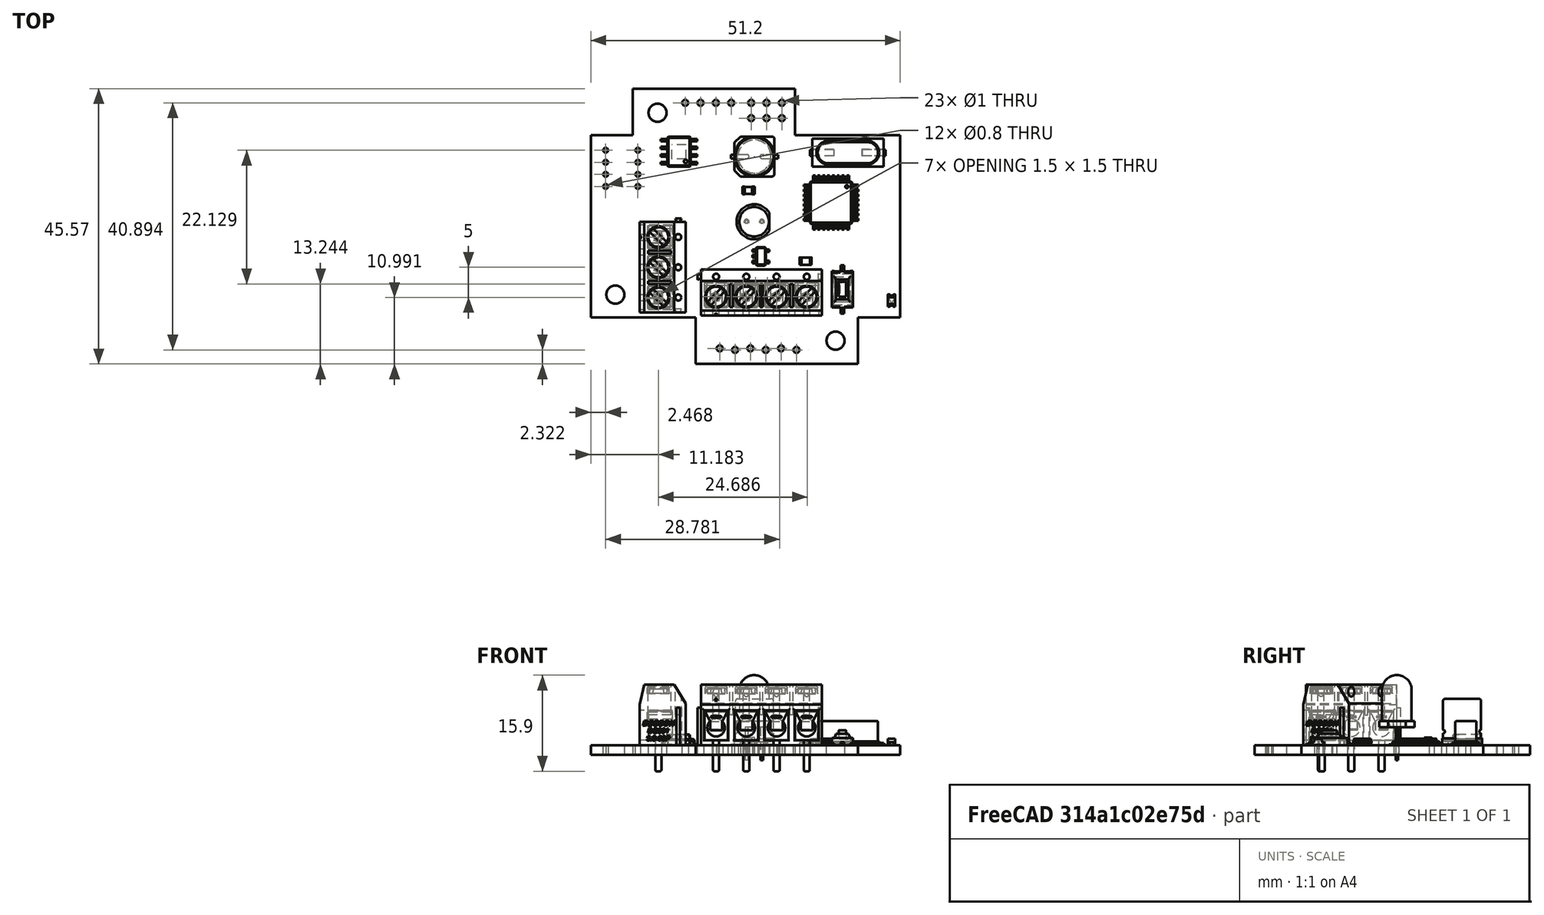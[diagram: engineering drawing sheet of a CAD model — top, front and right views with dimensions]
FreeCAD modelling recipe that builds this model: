
FCSTD DOCUMENT  (FreeCAD 0.19R24291 (Git))
Label: SolarSensorATMEGA328_PCB_freeCAD
License: All rights reserved
LicenseURL: http://en.wikipedia.org/wiki/All_rights_reserved
objects: App::Link×16, Part::Feature×13, App::Part×6, PartDesign::CoordinateSystem×1, Sketcher::SketchObject×1
note: 15 computed .brp shape members not serialized (recipe doc carries the construction recipe); baked Part::Feature solids carry a one-line shape summary decoded from their .brp

FEATURE [PartDesign::CoordinateSystem] Local_CS_ab9b
  AttacherType = Attacher::AttachEngine3D
FEATURE [Part::Feature] Pcb_ab9b
  shape: bbox 51.19 x 45.57 x 1.6 mm, 54 faces (baked)
FEATURE [Sketcher::SketchObject] PCB_Sketch_ab9b
  FullyConstrained = true
FEATURE [App::Part] Board_Geoms_ab9b
  Group = -> [Local_CS_ab9b,Pcb_ab9b,PCB_Sketch_ab9b]
  Origin = -> Origin
FEATURE [Part::Feature] Shape  label="SW2_SW_SPST_CK_RS282G05A3_60F30811"
  Placement = pos=(134.468,-118.745,0) rot=(0,0,-1;1.5708rad)
  shape: bbox 3.5 x 8 x 2.5 mm, 109 faces (baked)
FEATURE [App::Link] SW2_SW_SPST_CK_RS282G05A3_60F30811_ln_  label="SW1_SW_SPST_CK_RS282G05A3_60F354E5"
  LinkPlacement = pos=(139.065,-118.745,0) rot=(0,0,-1;1.5708rad)
  LinkedObject = -> Shape
  Placement = pos=(139.065,-118.745,0) rot=(0,0,-1;1.5708rad)
FEATURE [Part::Feature] Shape001  label="D2_LED_0805_2012Metric_Castellated_60F53ACF"
  Placement = pos=(142.621,-120.617,0) rot=(0,0,1;1.5708rad)
  shape: bbox 1.25 x 2 x 1.1 mm, 38 faces (baked)
FEATURE [Part::Feature] Shape002  label="R7_R_0805_2012Metric_60F30805"
  Placement = pos=(128.397,-114.096,0) rot=(0,0,1;0rad)
  shape: bbox 2 x 1.2 x 0.45 mm, 26 faces (baked)
FEATURE [App::Link] R7_R_0805_2012Metric_60F30805_ln_  label="R1_R_0805_2012Metric_60F3722D"
  LinkPlacement = pos=(114.758,-112.949,0) rot=(0,0,-1;1.5708rad)
  LinkedObject = -> Shape002
  Placement = pos=(114.758,-112.949,0) rot=(0,0,-1;1.5708rad)
FEATURE [App::Link] R7_R_0805_2012Metric_60F30805_ln_001  label="R4_R_0805_2012Metric_60F37335"
  LinkPlacement = pos=(142.571,-113.589,0) rot=(0,0,-1;1.5708rad)
  LinkedObject = -> Shape002
  Placement = pos=(142.571,-113.589,0) rot=(0,0,-1;1.5708rad)
FEATURE [App::Link] R7_R_0805_2012Metric_60F30805_ln_002  label="R5_R_0805_2012Metric_60F373AA"
  LinkPlacement = pos=(134.443,-112.319,0) rot=(0,0,-1;1.5708rad)
  LinkedObject = -> Shape002
  Placement = pos=(134.443,-112.319,0) rot=(0,0,-1;1.5708rad)
FEATURE [App::Link] R7_R_0805_2012Metric_60F30805_ln_003  label="R6_R_0805_2012Metric_60F35493"
  LinkPlacement = pos=(128.448,-111.556,0) rot=(0,0,1;0rad)
  LinkedObject = -> Shape002
  Placement = pos=(128.448,-111.556,0) rot=(0,0,1;0rad)
FEATURE [App::Link] R7_R_0805_2012Metric_60F30805_ln_004  label="R2_R_0805_2012Metric_61BC8E5A"
  LinkPlacement = pos=(112.218,-112.949,0) rot=(0,0,-1;1.5708rad)
  LinkedObject = -> Shape002
  Placement = pos=(112.218,-112.949,0) rot=(0,0,-1;1.5708rad)
FEATURE [Part::Feature] Shape003  label="C7_C_0805_2012Metric_60F30728[2]"
  Placement = pos=(118.948,-102.389,0) rot=(0,0,1;3.14159rad)
  shape: bbox 2 x 1.25 x 1.25 mm, 28 faces (baked)
FEATURE [App::Link] C7_C_0805_2012Metric_60F30728_2__ln_  label="C8_C_0805_2012Metric_60F30734[2]"
  LinkPlacement = pos=(109.447,-120.467,0) rot=(0,0,1;1.5708rad)
  LinkedObject = -> Shape003
  Placement = pos=(109.447,-120.467,0) rot=(0,0,1;1.5708rad)
FEATURE [App::Link] C7_C_0805_2012Metric_60F30728_2__ln_001  label="C9_C_0805_2012Metric_60F30740[2]"
  LinkPlacement = pos=(139.883,-100.049,0) rot=(0,0,1;0rad)
  LinkedObject = -> Shape003
  Placement = pos=(139.883,-100.049,0) rot=(0,0,1;0rad)
FEATURE [App::Link] C7_C_0805_2012Metric_60F30728_2__ln_002  label="C10_C_0805_2012Metric_60F3074C[2]"
  LinkPlacement = pos=(126.338,-97.0992,0) rot=(0,0,1;1.5708rad)
  LinkedObject = -> Shape003
  Placement = pos=(126.338,-97.0992,0) rot=(0,0,1;1.5708rad)
FEATURE [App::Link] C7_C_0805_2012Metric_60F30728_2__ln_003  label="C1_C_0805_2012Metric_60F372F7[2]"
  LinkPlacement = pos=(117.248,-112.954,0) rot=(0,0,-1;1.5708rad)
  LinkedObject = -> Shape003
  Placement = pos=(117.248,-112.954,0) rot=(0,0,-1;1.5708rad)
FEATURE [App::Link] C7_C_0805_2012Metric_60F30728_2__ln_004  label="C2_C_0805_2012Metric_60F37318[2]"
  LinkPlacement = pos=(114.478,-107.034,0) rot=(0,0,1;0rad)
  LinkedObject = -> Shape003
  Placement = pos=(114.478,-107.034,0) rot=(0,0,1;0rad)
FEATURE [App::Link] C7_C_0805_2012Metric_60F30728_2__ln_005  label="C3_C_0805_2012Metric_60F373E4[2]"
  LinkPlacement = pos=(114.073,-102.794,0) rot=(0,0,-1;1.5708rad)
  LinkedObject = -> Shape003
  Placement = pos=(114.073,-102.794,0) rot=(0,0,-1;1.5708rad)
FEATURE [App::Link] C7_C_0805_2012Metric_60F30728_2__ln_006  label="C4_C_0805_2012Metric_60F373C3[2]"
  LinkPlacement = pos=(109.423,-91.594,0) rot=(0,0,1;3.14159rad)
  LinkedObject = -> Shape003
  Placement = pos=(109.423,-91.594,0) rot=(0,0,1;3.14159rad)
FEATURE [App::Link] C7_C_0805_2012Metric_60F30728_2__ln_007  label="C5_C_0805_2012Metric_60F327E9[2]"
  LinkPlacement = pos=(123.063,-102.589,0) rot=(0,0,1;0rad)
  LinkedObject = -> Shape003
  Placement = pos=(123.063,-102.589,0) rot=(0,0,1;0rad)
FEATURE [App::Link] C7_C_0805_2012Metric_60F30728_2__ln_008  label="C11_C_0805_2012Metric_61C377F6[2]"
  LinkPlacement = pos=(109.828,-112.979,0) rot=(0,0,1;1.5708rad)
  LinkedObject = -> Shape003
  Placement = pos=(109.828,-112.979,0) rot=(0,0,1;1.5708rad)
FEATURE [Part::Feature] Shape004  label="U4_TQFP_32_7x7mm_P08mm_60F30876"
  Placement = pos=(132.588,-104.394,0) rot=(0,0,-1;1.5708rad)
  shape: bbox 9 x 9 x 1.1 mm, 524 faces (baked)
FEATURE [Part::Feature] Shape005  label="P2_DG301-5.0-04P-12-00AH_60F301A6"
  Placement = pos=(111.079,-115.467,0) rot=(1,0,0;1.5708rad)
  shape: bbox 20.6 x 7.6 x 14.3 mm, 562 faces (baked)
FEATURE [Part::Feature] Shape006  label="U1_TSOP_5_165x305mm_P095mm_60F30822"
  Placement = pos=(121.003,-113.284,0) rot=(0,0,1;0rad)
  shape: bbox 2.8 x 3.05 x 1.1 mm, 111 faces (baked)
FEATURE [Part::Feature] Shape007  label="Y1_Crystal_SMD_HC49-SD_60F3089C"
  Placement = pos=(135.382,-96.139,0) rot=(0,0,1;3.14159rad)
  shape: bbox 12.5 x 4.65 x 4 mm, 45 faces (baked)
FEATURE [Part::Feature] Shape008  label="C6_C_Elec_63x77_60F3729F"
  Placement = pos=(119.928,-96.774,0) rot=(0,0,1;0rad)
  shape: bbox 8.606 x 8.603 x 7.7 mm, 41 faces, 2 solids (baked)
FEATURE [Part::Feature] Shape009  label="U3_SOIC_8_1EP_39x49mm_P127mm_60F308EF"
  Placement = pos=(107.436,-95.977,0) rot=(0,0,1;3.14159rad)
  shape: bbox 6 x 4.9 x 1.75 mm, 161 faces (baked)
FEATURE [App::Link] U3_SOIC_8_1EP_39x49mm_P127mm_60F308EF_ln_  label="U2_SOIC_8_1EP_39x49mm_P127mm_60F52F81"
  LinkPlacement = pos=(107.448,-103.089,0) rot=(0,0,1;3.14159rad)
  LinkedObject = -> Shape009
  Placement = pos=(107.448,-103.089,0) rot=(0,0,1;3.14159rad)
FEATURE [Part::Feature] Shape010  label="J1_DG301-5.0-03P-12-00AH_61BC8E52"
  Placement = pos=(108.513,-107.609,0) rot=(-0.57735,0.57735,0.57735;4.18879rad)
  shape: bbox 7.6 x 15.6 x 14.3 mm, 491 faces (baked)
FEATURE [App::Part] Top_ab9b
  Group = -> [Shape,SW2_SW_SPST_CK_RS282G05A3_60F30811_ln_,Shape001,Shape002,R7_R_0805_2012Metric_60F30805_ln_,R7_R_0805_2012Metric_60F30805_ln_001,R7_R_0805_2012Metric_60F30805_ln_002,R7_R_0805_2012Metric_60F30805_ln_003,R7_R_0805_2012Metric_60F30805_ln_004,Shape003,C7_C_0805_2012Metric_60F30728_2__ln_,C7_C_0805_2012Metric_60F30728_2__ln_001,C7_C_0805_2012Metric_60F30728_2__ln_002,+14 more]
  Origin = -> Origin003
FEATURE [App::Part] Step_Models_ab9b
  Group = -> [Top_ab9b]
  Origin = -> Origin002
FEATURE [Part::Feature] Shape011  label="D1_LED_D5.0mm_Clear_61C65468"
  Placement = pos=(121.138,-107.569,0) rot=(0,0,1;3.14159rad)
  shape: bbox 5.4 x 5.8 x 14.1 mm, 16 faces (baked)
FEATURE [App::Part] TopV_ab9b
  Group = -> [Shape011]
  Origin = -> Origin006
FEATURE [App::Part] Step_Virtual_Models_ab9b
  Group = -> [TopV_ab9b]
  Origin = -> Origin005
FEATURE [App::Part] Board_ab9b  label="SolarSensorATMEGA328_PCB"
  Group = -> [Board_Geoms_ab9b,Step_Models_ab9b,Step_Virtual_Models_ab9b]
  Origin = -> Origin001
